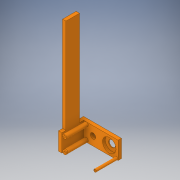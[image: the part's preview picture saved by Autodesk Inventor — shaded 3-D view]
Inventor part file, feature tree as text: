
AUTODESK INVENTOR PART (.ipt)
format: ipt  version: 2017 (Build 210142000, 142)  size: 216,064 bytes
history: native  units: in
note: dims shown in document units (in); Inventor stores cm internally (conversion verified against a paired STEP export)
features: extrude x12, sketch x12
ambient origin geometry x8: Origin, YZ Plane, XZ Plane, XY Plane, X Axis, Y Axis, Z Axis, Center Point
bodies: Solid1 (feature_tree)
feature tree (24):
  extrude  "Extrusion1"  Depth=1.3in
  extrude  "Extrusion2"  Depth=0.25in
  extrude  "Extrusion3"  Depth=1.05in
  extrude  "Extrusion14"  Depth=1.0in
  extrude  "Extrusion15"  Depth=0.5in
  extrude  "Extrusion16"  Depth=0.5in TaperAngle=0.0deg
  extrude  "Extrusion17"  Depth=0.15in
  extrude  "Extrusion18"  Depth=0.15in
  extrude  "Extrusion20"  Depth=0.3in
  extrude  "Extrusion21"  Depth=0.13in
  extrude  "Extrusion23"  Depth=0.2in
  extrude  "Extrusion24"  Depth=0.1in
  sketch  "Sketch1"  dims[d0=2.0in d1=1.3in]
  sketch  "Sketch2"  dims[d2=0.25in d3=0.0in d4=0.65in]
  sketch  "Sketch3"  dims[d5=0.65in d6=1.05in]
  sketch  "Sketch14"  dims[d7=0.3in d8=1.0in]
  sketch  "Sketch15"  dims[d9=0.2in d10=0.0in d11=0.5in]
  sketch  "Sketch16"  dims[d12=0.2in d13=0.0in d56=0.5in d57=0.0in]
  sketch  "Sketch17"  dims[d58=0.15in d59=0.15in]
  sketch  "Sketch18"  dims[d60=0.15in d61=0.15in]
  sketch  "Sketch20"  dims[d62=0.3in d63=0.3in]
  sketch  "Sketch21"  dims[d64=0.13in d65=0.13in]
  sketch  "Sketch23"  dims[d66=1.5in d67=0.0in d68=0.2in]
  sketch  "Sketch24"  dims[d69=0.1in d70=0.1in d71=0.13in d72=1.5in d73=0.0in d74=0.13in d75=0.3in d76=0.13in d77=0.3in d78=0.2in d79=0.1in d80=0.0in d81=0.5in d82=0.0in d86=0.2in d87=0.0in d88=0.25in d89=1.3in d90=1.6in d91=0.0in d94=1.0in d95=0.25in d96=0.3in d97=7.0in d98=0.0in d99=0.4in d100=1.2in d101=0.65in d102=1.0in d103=0.0in]
